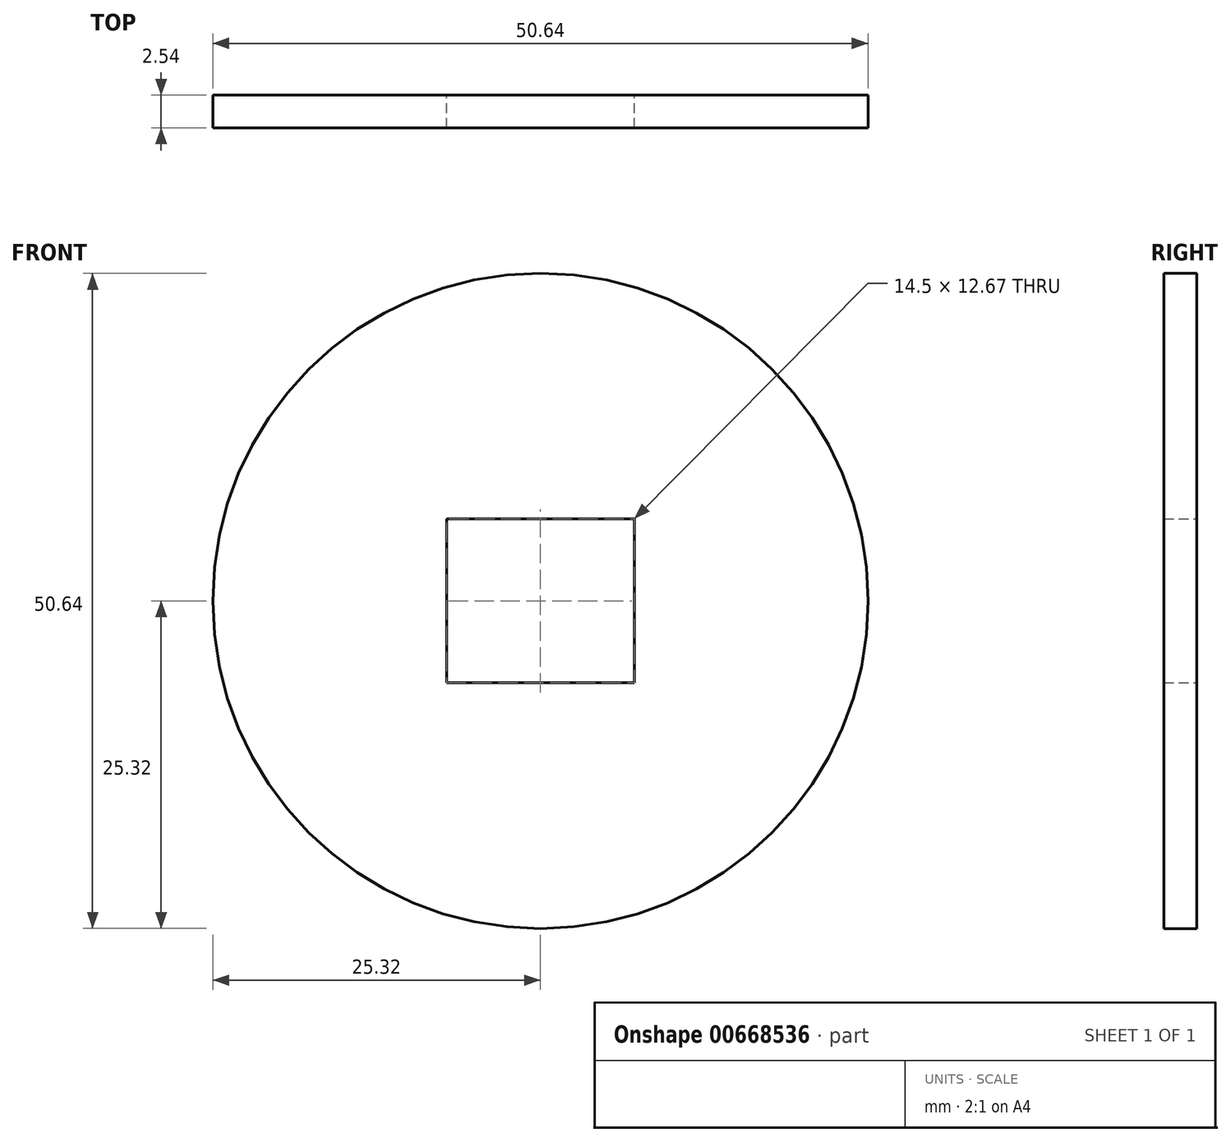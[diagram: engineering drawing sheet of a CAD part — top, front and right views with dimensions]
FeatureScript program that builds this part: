
annotation { "Feature Type Name" : "Feature", "Feature Type Description" : "" }
export const myFeature = defineFeature(function(context is Context, id is Id, definition is map)
    precondition{}
    {
        {
            var Q0;
            Q0=qCreatedBy(makeId("Front.planeOp"),FACE);
            var sketch = newSketch(context, id + "F0", { "sketchPlane" : qUnion([Q0])});
            skCircle(sketch, "E0", {"center": v(0, 0) * mm, "radius": 25.32 * mm});
            skLineSegment(sketch, "E1.bottom", {"start": v(-7.25, 6.34) * mm, "end": v(7.25, 6.34) * mm});
            skLineSegment(sketch, "E1.top", {"start": v(-7.25, -6.34) * mm, "end": v(7.25, -6.34) * mm});
            skLineSegment(sketch, "E1.left", {"start": v(-7.25, 6.34) * mm, "end": v(-7.25, -6.34) * mm});
            skLineSegment(sketch, "E1.right", {"start": v(7.25, 6.34) * mm, "end": v(7.25, -6.34) * mm});
            skSolve(sketch);
        }
        {
            var Q0;
            Q0=makeQuery(id+"F0.imprint","IMPRINT",FACE,{"disambiguationData":[TD([[makeQuery(id+"F0.imprint","IMPRINT",EDGE,{"derivedFrom":sQuery(id+"F0.wireOp",EDGE,"E0")}),1.0]])]});
            extrude(context, id + "F1", {"entities" : qUnion([Q0]), "depth" : 2.54 * mm, "offsetDistance" : 25.4 * mm});
        }
    });
